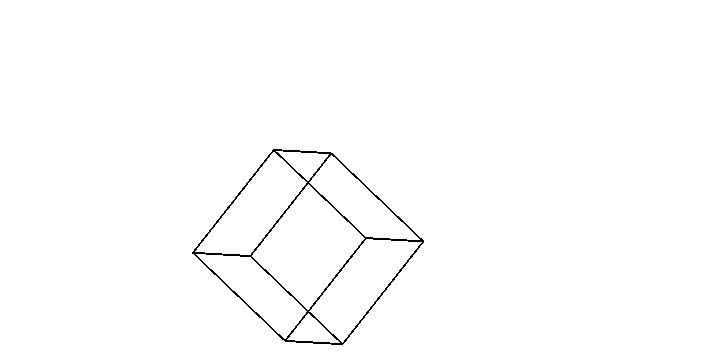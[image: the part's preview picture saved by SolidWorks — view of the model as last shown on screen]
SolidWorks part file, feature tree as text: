
SOLIDWORKS PART (.sldprt)
format: sldprt  version: not decoded by parser v0  size: 234,496 bytes
history: native  units: mm
features: sketch x5, plane x4, extrude x4, mirror x1 (+7 scaffold rows collapsed)
feature tree (21):
  scaffold x7  (default folders/planes/origin — collapsed)
  plane  "Face"
  plane  "Dessus"
  plane  "Droite"
  sketch  "Esquisse1"  dims[D1=0.1mm D2=0.1mm D3=0.05mm D4=0.05mm]
  extrude  "Extrusion1"  Depth=20mm
  sketch  "Esquisse3"  dims[D1=0.1mm D2=0.1mm]
  extrude  "Extrusion2"  Depth=19.9mm
  sketch  "Esquisse4"  dims[D1=0.1mm]
  extrude  "Extrusion3"  [1 undecoded]
  sketch  "Esquisse5"
  extrude  "Extrusion4"  Depth=9.9mm
  mirror  "Symétrie3"
  plane  "Plan1"
  sketch  "Esquisse6"
decode coverage: 6 of 10 modeling features carry decoded parameters
note: 1 parameter value undecoded
note: suppression state not decoded; provenance and decode notes live in map.json
